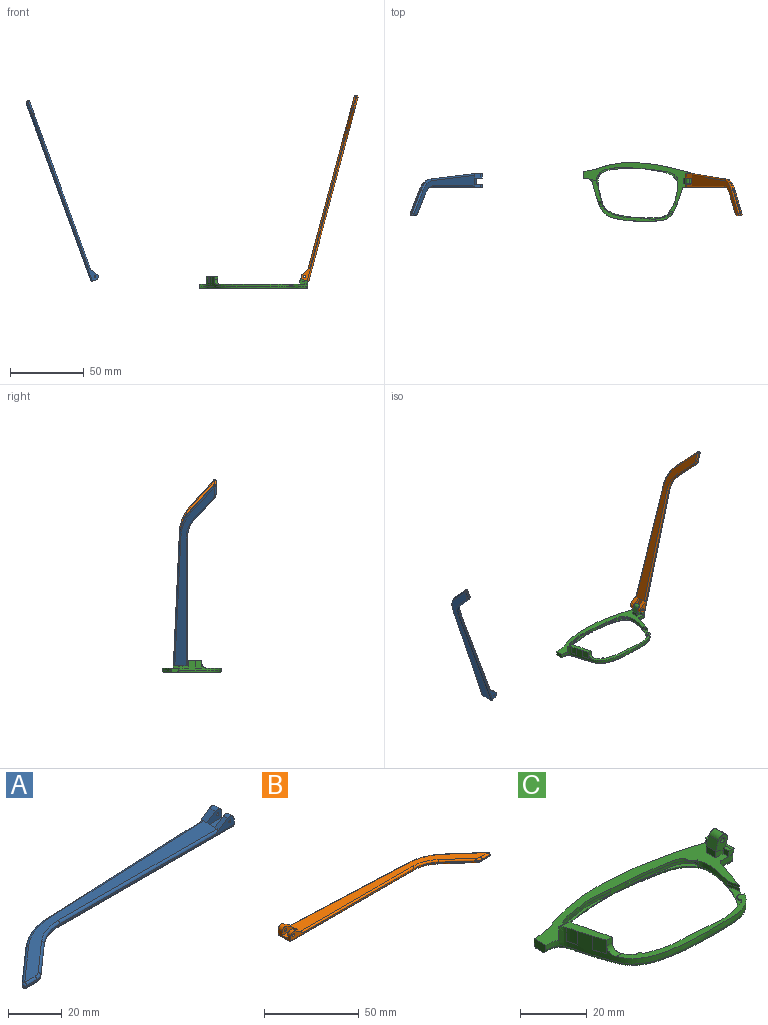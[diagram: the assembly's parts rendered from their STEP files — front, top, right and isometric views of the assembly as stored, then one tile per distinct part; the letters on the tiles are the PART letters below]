
ASSEMBLY  parts=3 mates=1
PART A: 43 faces, bbox 130.2x29.5x5.9 mm
  f0: plane 9.62x3.72mm, normal (1,0,0), area 24.7mm2, adj f1,f3,f4,f5,f10,f16,f18,f28
  f1: cylinder r=2.2mm len=3.45mm, axis (0,-1,0), area 11mm2, adj f0,f2,f4,f37
  f2: plane 6.01x3.91mm, normal (-0.55,0,0.84), area 12.7mm2, adj f1,f4,f9,f19,f37
  f3: plane 2.26x0.1mm, normal (0,0,1), area 0.1mm2, adj f0,f5,f18
  f4: plane 92.1x4.9mm, normal (0,-1,0), area 79.9mm2, adj f0,f1,f2,f14,f19,f36,f42
  f5: plane 93.42x4.13mm, normal (-0.04,1,0), area 64.8mm2, adj f0,f3,f11,f15,f17,f27,f28
  f6: plane 17.82x15.72mm, normal (-0.66,0.75,0), area 14.3mm2, adj f11,f12,f25,f30
  f7: plane 5.46x0.6mm, normal (0,-1,0), area 3.3mm2, adj f12,f13,f23,f32
  f8: plane 14.99x13.23mm, normal (0.66,-0.75,0), area 12mm2, adj f13,f14,f21,f34
  f9: plane 121.18x26.73mm, normal (0,0,1), area 627.7mm2, adj f2,f17,f19,f20,f21,f22,f23,f25
  f10: plane 129.1x27.08mm, normal (0,0,-1), area 686.5mm2, adj f0,f28,f29,f30,f32,f33,f34,f35
  f11: cylinder r=30mm len=18.52mm, axis (0,0,-1), area 12.2mm2, adj f5,f6,f26,f29
  f12: cylinder r=1mm len=1.75mm, axis (0,0,-1), area 1.5mm2, adj f6,f7,f24,f31
  f13: cylinder r=5mm len=3.31mm, axis (0,0,-1), area 2.2mm2, adj f7,f8,f22,f33
  f14: cylinder r=20mm len=13.23mm, axis (0,0,1), area 8.7mm2, adj f4,f8,f20,f35
  f15: plane 5.66x0.25mm, normal (0,0,-1), area 0.7mm2, adj f5,f17,f18
  f16: cylinder r=2.2mm len=3.45mm, axis (0,-1,0), area 14.8mm2, adj f0,f17,f18,f38
  f17: plane 6.01x3.91mm, normal (-0.55,0,0.84), area 16.9mm2, adj f5,f9,f15,f16,f18,f27,f38
  f18: plane 7.92x3.3mm, normal (0,1,0), area 15.9mm2, adj f0,f3,f15,f16,f17,f41
  f19: cylinder r=1mm len=84.18mm, axis (-1,0,0), area 131.4mm2, adj f2,f4,f9,f20
  f20: torus R=21mm, axis (0,0,1), area 23.1mm2, adj f9,f14,f19,f21
  f21: cylinder r=1mm len=15.65mm, axis (-0.75,-0.66,0), area 31.4mm2, adj f8,f9,f20,f22
  f22: torus R=4mm, axis (0,0,1), area 5.3mm2, adj f9,f13,f21,f23
  f23: cylinder r=1mm len=5.46mm, axis (-1,0,0), area 8.6mm2, adj f7,f9,f22,f24
  f24: sphere r=1mm, area 2.4mm2, adj f12,f23,f25
  f25: cylinder r=1mm len=18.48mm, axis (0.75,0.66,0), area 37.3mm2, adj f6,f9,f24,f26
  f26: torus R=29mm, axis (0,0,1), area 31.6mm2, adj f9,f11,f25,f27
  f27: cylinder r=1mm len=85.5mm, axis (1,0.04,0), area 133.5mm2, adj f5,f9,f17,f26
  f28: cylinder r=1mm len=93.46mm, axis (-1,-0.04,0), area 146.9mm2, adj f0,f5,f10,f29
  f29: torus R=29mm, axis (0,0,1), area 31.6mm2, adj f10,f11,f28,f30
  f30: cylinder r=1mm len=18.48mm, axis (-0.75,-0.66,0), area 37.3mm2, adj f6,f10,f29,f31
  f31: sphere r=1mm, area 2.4mm2, adj f12,f30,f32
  f32: cylinder r=1mm len=5.46mm, axis (1,0,0), area 8.6mm2, adj f7,f10,f31,f33
  f33: torus R=4mm, axis (0,0,1), area 5.3mm2, adj f10,f13,f32,f34
  f34: cylinder r=1mm len=15.65mm, axis (0.75,0.66,0), area 31.4mm2, adj f8,f10,f33,f35
  f35: torus R=21mm, axis (0,0,1), area 23.1mm2, adj f10,f14,f34,f36
  f36: cylinder r=1mm len=92.1mm, axis (1,0,0), area 144.7mm2, adj f0,f4,f10,f35
  f37: plane 7.92x4.7mm, normal (0,1,0), area 27mm2, adj f0,f1,f2,f39,f40,f42
  f38: plane 7.92x4.7mm, normal (0,-1,0), area 27mm2, adj f0,f16,f17,f39,f40,f41
  f39: plane 7.92x4.1mm, normal (0,0,1), area 32.5mm2, adj f0,f37,f38,f40
  f40: plane 4.1x1.4mm, normal (1,0,0), area 5.7mm2, adj f9,f37,f38,f39
  f41: cylinder r=0.5mm len=3.1mm, axis (0,-1,0), area 9.7mm2, adj f18,f38
  f42: cylinder r=0.5mm len=2.3mm, axis (0,-1,0), area 7.2mm2, adj f4,f37
PART B: 43 faces, bbox 130.2x29.5x5.9 mm
  f0: plane 9.62x3.72mm, normal (-1,0,0), area 24.7mm2, adj f1,f3,f4,f5,f10,f16,f18,f28
  f1: cylinder r=2.2mm len=3.45mm, axis (0,-1,0), area 11mm2, adj f0,f2,f4,f37
  f2: plane 6.01x3.91mm, normal (0.55,0,0.84), area 12.7mm2, adj f1,f4,f9,f19,f37
  f3: plane 2.26x0.1mm, normal (0,0,1), area 0.1mm2, adj f0,f5,f18
  f4: plane 92.1x4.9mm, normal (0,-1,0), area 78.2mm2, adj f0,f1,f2,f14,f19,f36,f42
  f5: plane 93.42x4.13mm, normal (0.04,1,0), area 64.8mm2, adj f0,f3,f11,f15,f17,f27,f28
  f6: plane 17.82x15.72mm, normal (0.66,0.75,0), area 14.3mm2, adj f11,f12,f25,f30
  f7: plane 5.46x0.6mm, normal (0,-1,0), area 3.3mm2, adj f12,f13,f23,f32
  f8: plane 14.99x13.23mm, normal (-0.66,-0.75,0), area 12mm2, adj f13,f14,f21,f34
  f9: plane 121.18x26.73mm, normal (0,0,1), area 627.7mm2, adj f2,f17,f19,f20,f21,f22,f23,f25
  f10: plane 129.1x27.08mm, normal (0,0,-1), area 686.5mm2, adj f0,f28,f29,f30,f32,f33,f34,f35
  f11: cylinder r=30mm len=18.52mm, axis (0,0,-1), area 12.2mm2, adj f5,f6,f26,f29
  f12: cylinder r=1mm len=1.75mm, axis (0,0,-1), area 1.5mm2, adj f6,f7,f24,f31
  f13: cylinder r=5mm len=3.31mm, axis (0,0,-1), area 2.2mm2, adj f7,f8,f22,f33
  f14: cylinder r=20mm len=13.23mm, axis (0,0,1), area 8.7mm2, adj f4,f8,f20,f35
  f15: plane 5.66x0.25mm, normal (0,0,-1), area 0.7mm2, adj f5,f17,f18
  f16: cylinder r=2.2mm len=3.45mm, axis (0,-1,0), area 14.8mm2, adj f0,f17,f18,f38
  f17: plane 6.01x3.91mm, normal (0.55,0,0.84), area 16.9mm2, adj f5,f9,f15,f16,f18,f27,f38
  f18: plane 7.92x3.3mm, normal (0,1,0), area 14.3mm2, adj f0,f3,f15,f16,f17,f41
  f19: cylinder r=1mm len=84.18mm, axis (1,0,0), area 131.4mm2, adj f2,f4,f9,f20
  f20: torus R=21mm, axis (0,0,1), area 23.1mm2, adj f9,f14,f19,f21
  f21: cylinder r=1mm len=15.65mm, axis (0.75,-0.66,0), area 31.4mm2, adj f8,f9,f20,f22
  f22: torus R=4mm, axis (0,0,1), area 5.3mm2, adj f9,f13,f21,f23
  f23: cylinder r=1mm len=5.46mm, axis (1,0,0), area 8.6mm2, adj f7,f9,f22,f24
  f24: sphere r=1mm, area 2.4mm2, adj f12,f23,f25
  f25: cylinder r=1mm len=18.48mm, axis (-0.75,0.66,0), area 37.3mm2, adj f6,f9,f24,f26
  f26: torus R=29mm, axis (0,0,1), area 31.6mm2, adj f9,f11,f25,f27
  f27: cylinder r=1mm len=85.5mm, axis (-1,0.04,0), area 133.5mm2, adj f5,f9,f17,f26
  f28: cylinder r=1mm len=93.46mm, axis (1,-0.04,0), area 146.9mm2, adj f0,f5,f10,f29
  f29: torus R=29mm, axis (0,0,1), area 31.6mm2, adj f10,f11,f28,f30
  f30: cylinder r=1mm len=18.48mm, axis (0.75,-0.66,0), area 37.3mm2, adj f6,f10,f29,f31
  f31: sphere r=1mm, area 2.4mm2, adj f12,f30,f32
  f32: cylinder r=1mm len=5.46mm, axis (-1,0,0), area 8.6mm2, adj f7,f10,f31,f33
  f33: torus R=4mm, axis (0,0,1), area 5.3mm2, adj f10,f13,f32,f34
  f34: cylinder r=1mm len=15.65mm, axis (-0.75,0.66,0), area 31.4mm2, adj f8,f10,f33,f35
  f35: torus R=21mm, axis (0,0,1), area 23.1mm2, adj f10,f14,f34,f36
  f36: cylinder r=1mm len=92.1mm, axis (-1,0,0), area 144.7mm2, adj f0,f4,f10,f35
  f37: plane 7.92x4.7mm, normal (0,1,0), area 25.4mm2, adj f0,f1,f2,f39,f40,f42
  f38: plane 7.92x4.7mm, normal (0,-1,0), area 25.4mm2, adj f0,f16,f17,f39,f40,f41
  f39: plane 7.92x4.1mm, normal (0,0,1), area 32.5mm2, adj f0,f37,f38,f40
  f40: plane 4.1x1.4mm, normal (-1,0,0), area 5.7mm2, adj f9,f37,f38,f39
  f41: cylinder r=0.88mm len=3.1mm, axis (0,-1,0), area 17mm2, adj f18,f38
  f42: cylinder r=0.88mm len=2.3mm, axis (0,-1,0), area 12.6mm2, adj f4,f37
PART C: 70 faces, bbox 75.1x41x10.6 mm
  f0: plane 3.72x1.06mm, normal (0,0,1), area 0.1mm2, adj f10,f58
  f1: plane 2.29x0.42mm, normal (0,0,1), area 0.1mm2, adj f23,f55
  f2: plane 9.92x2.4mm, normal (0,0,1), area 2.3mm2, adj f14,f23,f26,f54
  f3: plane 73.77x29.9mm, normal (0,0,1), area 347.2mm2, adj f5,f6,f7,f8,f9,f10,f11,f12
  f4: plane 50.32x10.36mm, normal (0,0,1), area 106.5mm2, adj f10,f26,f65,f67,f68
  f5: plane 1.23x0.04mm, normal (0,0,1), area 0mm2, adj f3,f11,f37
  f6: plane 6.97x5.07mm, normal (0,1,0), area 22.7mm2, adj f3,f35,f36,f40,f42,f43,f45,f46
  f7: plane 3.2x2.36mm, normal (0,-1,0), area 5.7mm2, adj f3,f35,f41,f44
  f8: extruded ~5.91x2mm, area 11.9mm2, adj f3,f16,f22,f23,f24,f34
  f9: extruded ~13.33x2mm, area 27.5mm2, adj f3,f16,f19,f24,f25,f34
  f10: extruded ~60.98x29.37mm, area 198.8mm2, adj f0,f3,f4,f13,f18,f26,f27,f31
  f11: extruded ~38.04x29.49mm, area 135.6mm2, adj f3,f5,f12,f19,f25,f29,f30,f31
  f12: extruded ~35.39x5.69mm, area 72.2mm2, adj f3,f11,f13,f28
  f13: plane 4.83x3.04mm, normal (-1,0,0), area 13.9mm2, adj f3,f10,f12,f15,f28,f31
  f14: extruded ~6.68x2mm, area 13.8mm2, adj f2,f18,f22,f23,f26,f34
  f15: plane 72.4x37.85mm, normal (0,0,-1), area 291mm2, adj f13,f28,f29,f31,f32,f34
  f16: extruded ~23.16x7.85mm, area 26.4mm2, adj f8,f9,f17,f24
  f17: plane 23.34x8.01mm, normal (0,0,1), area 17.5mm2, adj f16,f34
  f18: extruded ~48.97x13.52mm, area 56.4mm2, adj f10,f14,f20,f26
  f19: extruded ~4.15x1mm, area 4.2mm2, adj f9,f11,f20,f25
  f20: plane 51.32x13.99mm, normal (0,0,1), area 52.5mm2, adj f18,f19,f31,f34
  f21: plane 26.54x15.85mm, normal (0,0,1), area 28mm2, adj f22,f34
  f22: extruded ~25.74x15.11mm, area 36.5mm2, adj f8,f14,f21,f23
  f23: extruded ~25.74x15.11mm, area 47.1mm2, adj f1,f2,f3,f8,f14,f22,f54,f55
  f24: extruded ~23.16x7.85mm, area 24.5mm2, adj f3,f8,f9,f16,f62,f63
  f25: extruded ~4.15x1mm, area 4.2mm2, adj f3,f9,f11,f19
  f26: extruded ~48.97x13.52mm, area 56.1mm2, adj f2,f4,f10,f14,f18,f54,f64,f65
  f27: plane 4.46x1.45mm, normal (0,0,1), area 0.1mm2, adj f10,f52
  f28: bspline ~37.01x6.7mm, area 56.6mm2, adj f12,f13,f15,f29
  f29: bspline ~45.86x8.59mm, area 59.8mm2, adj f11,f15,f28,f30
  f30: bspline ~1.04x1mm, area 0.8mm2, adj f11,f29,f32
  f31: bspline ~73.09x30.38mm, area 161.7mm2, adj f10,f11,f13,f15,f20,f33
  f32: bspline ~8.61x1.2mm, area 12.6mm2, adj f11,f15,f30,f33
  f33: bspline ~1x1mm, area 0.8mm2, adj f11,f31,f32
  f34: bspline ~56.23x35.9mm, area 235.3mm2, adj f8,f9,f14,f15,f17,f20,f21
  f35: plane 4x2.36mm, normal (-1,0,0), area 9.5mm2, adj f3,f6,f7,f36
  f36: plane 4x0.02mm, normal (0.34,0,0.94), area 0.1mm2, adj f6,f35,f43
  f37: plane 2.76x2.53mm, normal (0,-1,0), area 3.9mm2, adj f5,f41,f42,f50,f69
  f38: plane 7.67x1.6mm, normal (0.94,0,-0.34), area 13mm2, adj f3,f50,f51,f69
  f39: plane 2.1x1.69mm, normal (0,1,0), area 2.8mm2, adj f3,f40,f42,f51,f69
  f40: plane 3.3x2.1mm, normal (-1,0,0), area 6.9mm2, adj f3,f6,f39,f42
  f41: plane 2.35x2.1mm, normal (-1,0,0), area 4.9mm2, adj f3,f7,f37,f42,f44
  f42: plane 9.65x1.24mm, normal (0,0,1), area 8.2mm2, adj f6,f37,f39,f40,f41,f44,f45,f69
  f43: plane 4x3.31mm, normal (-0.94,0,0.34), area 14.1mm2, adj f6,f36,f44,f47
  f44: plane 5.77x5.06mm, normal (0,-1,0), area 17mm2, adj f7,f41,f42,f43,f45,f46,f47,f48
  f45: plane 4x2.21mm, normal (0.94,0,-0.34), area 9.4mm2, adj f6,f42,f44,f48
  f46: plane 4x0.01mm, normal (0.34,0,0.94), area 0mm2, adj f6,f44,f47,f48
  f47: cylinder r=1.98mm len=4mm, axis (0,1,0), area 12.4mm2, adj f6,f43,f44,f46
  f48: cylinder r=1.98mm len=4mm, axis (0,-1,0), area 12.4mm2, adj f6,f44,f45,f46
  f49: cylinder r=0.88mm len=4mm, axis (0,-1,0), area 22mm2, adj f6,f44
  f50: cone r=1mm half-angle=20deg, axis (0,0,1), area 2.3mm2, adj f3,f37,f38,f69
  f51: cylinder r=1mm len=2.28mm, axis (-0.34,0,-0.94), area 3mm2, adj f3,f38,f39,f69
  f52: extruded ~5x4.44mm, area 23.3mm2, adj f10,f27,f59
  f53: plane 2.36x2mm, normal (0,-1,0), area 4.7mm2, adj f10,f54,f59,f68
  f54: extruded ~9.81x5mm, area 50.4mm2, adj f2,f23,f26,f53,f59
  f55: extruded ~5x2.27mm, area 11.6mm2, adj f1,f23,f56,f59
  f56: plane 5x4.19mm, normal (0.15,0.99,0), area 21.2mm2, adj f3,f55,f57,f59
  f57: extruded ~5x0.06mm, area 0.4mm2, adj f3,f10,f56,f59
  f58: extruded ~5x3.64mm, area 18.9mm2, adj f0,f10,f59
  f59: plane 15.07x7.57mm, normal (0,0,1), area 41.2mm2, adj f10,f23,f52,f53,f54,f55,f56,f57
  f60: plane 3.32x1.74mm, normal (0,0,-1), area 2.9mm2, adj f23,f61
  f61: cylinder r=2.28mm len=3.26mm, axis (0,0,1), area 2mm2, adj f3,f23,f60
  f62: plane 3.19x2.21mm, normal (0,0,-1), area 3.6mm2, adj f24,f63
  f63: cylinder r=2.28mm len=3.1mm, axis (0,0,1), area 2.1mm2, adj f3,f24,f62
  f64: plane 1.77x1.32mm, normal (0,0,-1), area 0.9mm2, adj f26,f65
  f65: cylinder r=1.3mm len=1.75mm, axis (0,0,1), area 1.3mm2, adj f4,f26,f64
  f66: plane 2.6x2.27mm, normal (0,0,-1), area 3.5mm2, adj f26,f67
  f67: cylinder r=1.3mm len=2.59mm, axis (0,0,1), area 2.5mm2, adj f4,f26,f66
  f68: cylinder r=3mm len=3.32mm, axis (1,0,0), area 10.7mm2, adj f4,f10,f26,f53
  f69: plane 9.71x1.44mm, normal (0.34,0,0.94), area 13.9mm2, adj f37,f38,f39,f42,f50,f51
PLACE A rot(axis=(0,1,0),70deg) t=(-84.77,-5.75,56)mm
PLACE B rot(axis=(0,-1,0),75deg) t=(68.2,-5.75,-61.61)mm
PLACE C t=(10.15,-1.13,-5.77)mm
MATE revolute B.f41 <-> C.f48  axis (0,-1,0) through (81.2,2.72,1.21)mm
